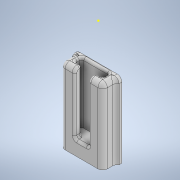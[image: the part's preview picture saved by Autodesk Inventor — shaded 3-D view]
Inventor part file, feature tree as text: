
AUTODESK INVENTOR PART (.ipt)
format: ipt  version: 2022 (Build 260153000, 153)  size: 570,880 bytes
history: native  units: mm
features: sketch x11, extrude x10, fillet x9
ambient origin geometry x8: Origin, YZ Plane, XZ Plane, XY Plane, X Axis, Y Axis, Z Axis, Center Point
bodies: Solid1 (feature_tree), Solid2 (feature_tree), Solid4 (feature_tree)
feature tree (30):
  extrude  "Extrusion1"  Depth=80.0mm
  extrude  "Extrusion2"  Depth=25.0mm
  extrude  "Extrusion3"  Depth=15.0mm
  fillet  "Fillet12"  Radius=15.0mm
  fillet  "Fillet1"  Radius=15.0mm
  extrude  "Extrusion4"  Depth=15.0mm
  fillet  "Fillet2"  Radius=15.0mm
  fillet  "Fillet4"  Radius=10.0mm
  extrude  "Extrusion5"  Depth=60.0mm TaperAngle=0.0deg
  extrude  "Extrusion11"  Depth=2.5mm
  extrude  "Extrusion12"  Depth=1.0mm
  extrude  "Extrusion13"  Depth=3.0mm
  extrude  "Extrusion14"  Depth=9.0mm TaperAngle=0.0deg
  extrude  "Extrusion15"  Depth=0.5mm
  fillet  "Fillet7"  Radius=50.0mm
  fillet  "Fillet8"  Radius=40.0mm
  fillet  "Fillet9"  Radius=25.0mm
  fillet  "Fillet10"  Radius=15.0mm
  fillet  "Fillet11"  Radius=100.0mm
  sketch  "Sketch18"  dims[d113=1.5mm d114=1.5mm d115=1.5mm d116=1.5mm d117=14.0mm d118=98.0mm d119=0.0mm d120=16.0mm d121=31.5mm d122=98.0mm d123=-1.745329mm d124=14.0mm d125=2.0mm d126=2.0mm d127=2.0mm d128=2.0mm d129=13.0mm d130=0.3mm d131=3.0mm d132=0.0mm d133=0.0mm d134=15.0mm d135=3.0mm d136=0.0mm d137=33.0mm d138=11.0mm d139=16.5mm d140=6.0mm d141=16.0mm d144=3.0mm d145=3.0mm d146=0.5mm d147=2.0mm d148=1.0mm d150=55.0mm d151=1.0mm d152=5.0mm]
  sketch  "Sketch1"  dims[d0=50.0mm d1=80.0mm]
  sketch  "Sketch2"  dims[d2=40.0mm d3=25.0mm]
  sketch  "Sketch4"  dims[d4=3.0mm d5=0.0mm d6=15.0mm d7=15.0mm d8=15.0mm]
  sketch  "Sketch5"  dims[d9=7.5mm d10=15.0mm d11=15.0mm d12=0.0mm d13=10.0mm]
  sketch  "Sketch6"  dims[d16=10.0mm d17=60.0mm d18=0.0mm]
  sketch  "Sketch13"  dims[d19=7.5mm d20=2.5mm]
  sketch  "Sketch14"  dims[d21=1.0mm d22=1.0mm]
  sketch  "Sketch15"  dims[d25=7.0mm d26=0.0mm d27=3.0mm]
  sketch  "Sketch16"  dims[d29=3.0mm d32=9.0mm d33=0.0mm]
  sketch  "Sketch17"  dims[d58=0.5mm d59=0.5mm d107=50.0mm d108=40.0mm d109=25.0mm d110=15.0mm d111=100.0mm d112=0.0mm]
